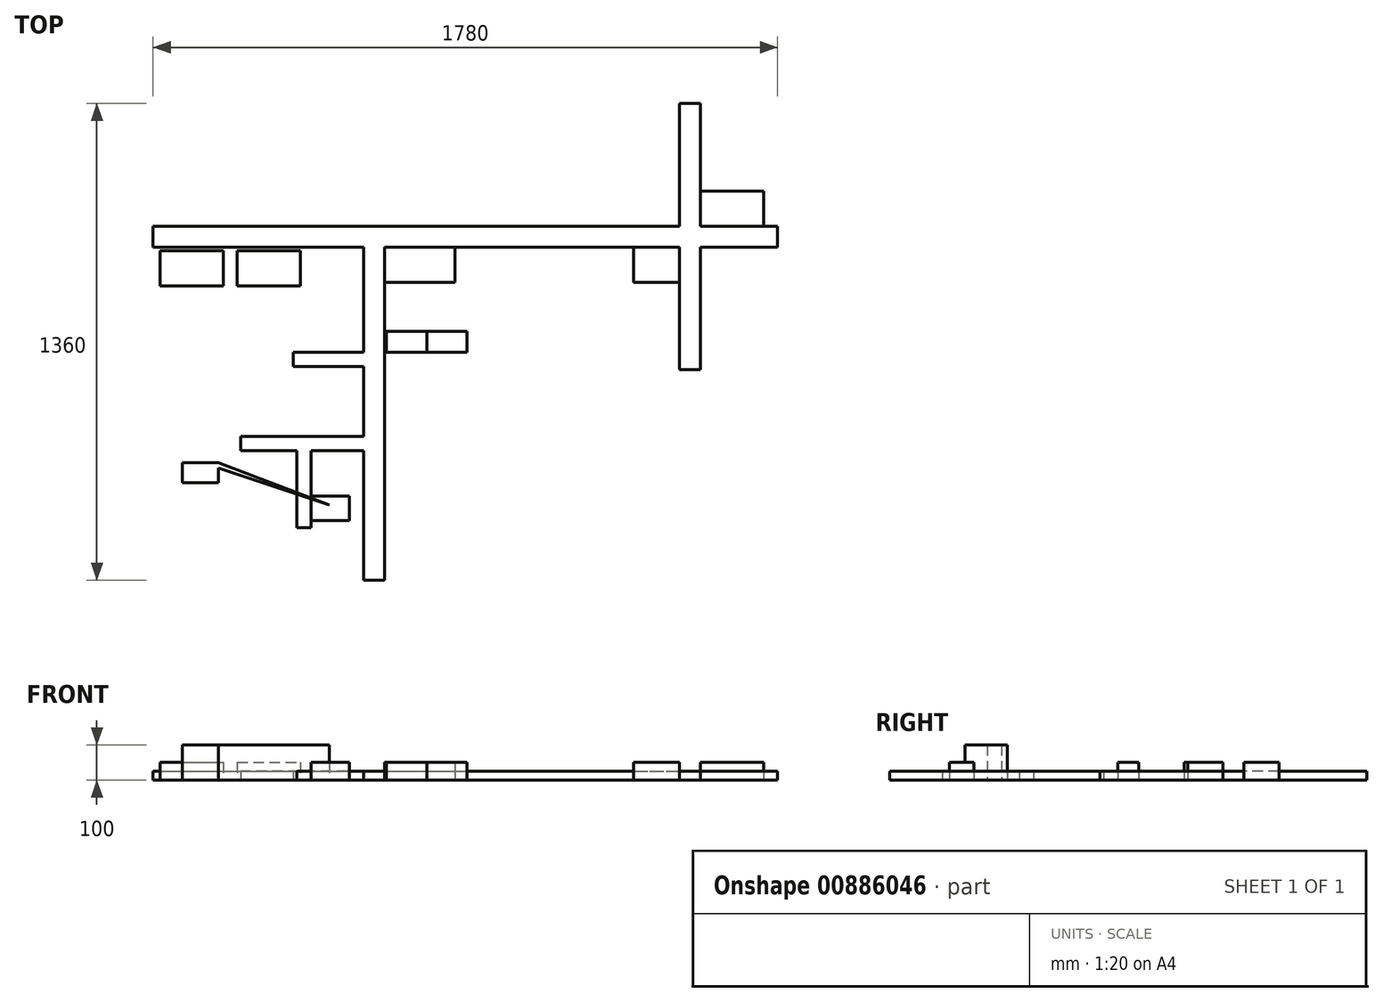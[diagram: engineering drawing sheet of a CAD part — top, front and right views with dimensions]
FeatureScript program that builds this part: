
annotation { "Feature Type Name" : "Feature", "Feature Type Description" : "" }
export const myFeature = defineFeature(function(context is Context, id is Id, definition is map)
    precondition{}
    {
        {
            var Q0;
            Q0=qCreatedBy(makeId("Top.planeOp"),FACE);
            var sketch = newSketch(context, id + "F0", { "sketchPlane" : qUnion([Q0])});
            skLineSegment(sketch, "E0", {"start": v(0, 0) * mm, "end": v(1500, 0) * mm});
            skLineSegment(sketch, "E1", {"start": v(1500, 0) * mm, "end": v(1500, 350) * mm});
            skLineSegment(sketch, "E2", {"start": v(1560, 350) * mm, "end": v(1560, 0) * mm});
            skLineSegment(sketch, "E3", {"start": v(1560, 0) * mm, "end": v(1780, 0) * mm});
            skLineSegment(sketch, "E4", {"start": v(0, -60) * mm, "end": v(600, -60) * mm});
            skLineSegment(sketch, "E5", {"start": v(600, -60) * mm, "end": v(600, -360) * mm});
            skLineSegment(sketch, "E6", {"start": v(600, -360) * mm, "end": v(400, -360) * mm});
            skLineSegment(sketch, "E7", {"start": v(400, -400) * mm, "end": v(600, -400) * mm});
            skLineSegment(sketch, "E8", {"start": v(600, -400) * mm, "end": v(600, -600) * mm});
            skLineSegment(sketch, "E9", {"start": v(600, -600) * mm, "end": v(250, -600) * mm});
            skLineSegment(sketch, "E10", {"start": v(250, -640) * mm, "end": v(410, -640) * mm});
            skLineSegment(sketch, "E11", {"start": v(410, -640) * mm, "end": v(410, -860) * mm});
            skLineSegment(sketch, "E12", {"start": v(450, -860) * mm, "end": v(450, -640) * mm});
            skLineSegment(sketch, "E13", {"start": v(450, -640) * mm, "end": v(600, -640) * mm});
            skLineSegment(sketch, "E14", {"start": v(600, -640) * mm, "end": v(600, -1010) * mm});
            skLineSegment(sketch, "E15", {"start": v(660, -1010) * mm, "end": v(660, -60) * mm});
            skLineSegment(sketch, "E16", {"start": v(660, -60) * mm, "end": v(1500, -60) * mm});
            skLineSegment(sketch, "E17", {"start": v(1500, -60) * mm, "end": v(1500, -410) * mm});
            skLineSegment(sketch, "E18", {"start": v(1560, -410) * mm, "end": v(1560, -60) * mm});
            skLineSegment(sketch, "E19", {"start": v(1560, -60) * mm, "end": v(1780, -60) * mm});
            skLineSegment(sketch, "E20", {"start": v(0, -60) * mm, "end": v(0, 0) * mm});
            skLineSegment(sketch, "E21", {"start": v(1500, -410) * mm, "end": v(1560, -410) * mm});
            skLineSegment(sketch, "E22", {"start": v(1780, 0) * mm, "end": v(1780, -60) * mm});
            skLineSegment(sketch, "E23", {"start": v(1500, 350) * mm, "end": v(1560, 350) * mm});
            skLineSegment(sketch, "E24", {"start": v(600, -1010) * mm, "end": v(660, -1010) * mm});
            skLineSegment(sketch, "E25", {"start": v(410, -860) * mm, "end": v(450, -860) * mm});
            skLineSegment(sketch, "E26", {"start": v(250, -640) * mm, "end": v(250, -600) * mm});
            skLineSegment(sketch, "E27", {"start": v(400, -400) * mm, "end": v(400, -360) * mm});
            skSolve(sketch);
        }
        {
            var Q0;
            Q0 = qSketchRegion(id + "F0", true);
            extrude(context, id + "F1", {"entities" : qUnion([Q0]), "depth" : 25 * mm, "offsetDistance" : 25 * mm});
        }
        {
            var Q0;
            Q0=qCreatedBy(makeId("Top.planeOp"),FACE);
            var sketch = newSketch(context, id + "F2", { "sketchPlane" : qUnion([Q0])});
            skLineSegment(sketch, "E28.0", {"start": v(1560, 0) * mm, "end": v(1740, 0) * mm});
            skLineSegment(sketch, "E28.1", {"start": v(1560, 100) * mm, "end": v(1560, 0) * mm});
            skLineSegment(sketch, "E29", {"start": v(1560, 100) * mm, "end": v(1740, 100) * mm});
            skLineSegment(sketch, "E30", {"start": v(1740, 100) * mm, "end": v(1740, 0) * mm});
            skLineSegment(sketch, "E31.0", {"start": v(1370, -60) * mm, "end": v(1500, -60) * mm});
            skLineSegment(sketch, "E32", {"start": v(1500, -60) * mm, "end": v(1500, -160) * mm});
            skLineSegment(sketch, "E33", {"start": v(1500, -160) * mm, "end": v(1370, -160) * mm});
            skLineSegment(sketch, "E34", {"start": v(1370, -160) * mm, "end": v(1370, -60) * mm});
            skLineSegment(sketch, "E35.0", {"start": v(660, -160) * mm, "end": v(660, -60) * mm});
            skLineSegment(sketch, "E36", {"start": v(660, -60) * mm, "end": v(860, -60) * mm});
            skLineSegment(sketch, "E37", {"start": v(860, -60) * mm, "end": v(860, -160) * mm});
            skLineSegment(sketch, "E38", {"start": v(860, -160) * mm, "end": v(660, -160) * mm});
            skLineSegment(sketch, "E39.bottom", {"start": v(665, -360) * mm, "end": v(895, -360) * mm});
            skLineSegment(sketch, "E39.top", {"start": v(665, -300) * mm, "end": v(895, -300) * mm});
            skLineSegment(sketch, "E39.left", {"start": v(665, -360) * mm, "end": v(665, -300) * mm});
            skLineSegment(sketch, "E39.right", {"start": v(895, -360) * mm, "end": v(895, -300) * mm});
            skLineSegment(sketch, "E40", {"start": v(780, -300) * mm, "end": v(780, -360) * mm});
            skLineSegment(sketch, "E41.0", {"start": v(450, -840) * mm, "end": v(450, -770) * mm});
            skLineSegment(sketch, "E42", {"start": v(450, -770) * mm, "end": v(560, -770) * mm});
            skLineSegment(sketch, "E43", {"start": v(560, -770) * mm, "end": v(560, -840) * mm});
            skLineSegment(sketch, "E44", {"start": v(560, -840) * mm, "end": v(450, -840) * mm});
            skLineSegment(sketch, "E45.bottom", {"start": v(20, -70) * mm, "end": v(200, -70) * mm});
            skLineSegment(sketch, "E45.top", {"start": v(20, -170) * mm, "end": v(200, -170) * mm});
            skLineSegment(sketch, "E45.left", {"start": v(20, -70) * mm, "end": v(20, -170) * mm});
            skLineSegment(sketch, "E45.right", {"start": v(200, -70) * mm, "end": v(200, -170) * mm});
            skLineSegment(sketch, "E46.bottom", {"start": v(240, -70) * mm, "end": v(420, -70) * mm});
            skLineSegment(sketch, "E46.top", {"start": v(240, -170) * mm, "end": v(420, -170) * mm});
            skLineSegment(sketch, "E46.left", {"start": v(240, -70) * mm, "end": v(240, -170) * mm});
            skLineSegment(sketch, "E46.right", {"start": v(420, -70) * mm, "end": v(420, -170) * mm});
            skSolve(sketch);
        }
        {
            var Q0;
            Q0=makeQuery(id+"F2.imprint","IMPRINT",FACE,{"disambiguationData":[TD([[makeQuery(id+"F2.imprint","IMPRINT",EDGE,{"derivedFrom":sQuery(id+"F2.wireOp",EDGE,"E45.bottom")}),-1.0]])]});
            var Q1;
            Q1=makeQuery(id+"F2.imprint","IMPRINT",FACE,{"disambiguationData":[TD([[makeQuery(id+"F2.imprint","IMPRINT",EDGE,{"derivedFrom":sQuery(id+"F2.wireOp",EDGE,"E46.bottom")}),-1.0]])]});
            var Q2;
            Q2=makeQuery(id+"F2.imprint","IMPRINT",FACE,{"disambiguationData":[TD([[makeQuery(id+"F2.imprint","IMPRINT",EDGE,{"derivedFrom":sQuery(id+"F2.wireOp",EDGE,"E35.0")}),-1.0]])]});
            var Q3;
            {var subQ0=sQuery(id+"F2.wireOp",EDGE,"E39.left");Q3=makeQuery(id+"F2.imprint","IMPRINT",FACE,{"disambiguationData":[TD([[makeQuery(id+"F2.imprint","IMPRINT",EDGE,{"derivedFrom":subQ0}),-1.0]])]});}
            var Q4;
            Q4=makeQuery(id+"F2.imprint","IMPRINT",FACE,{"disambiguationData":[TD([[makeQuery(id+"F2.imprint","IMPRINT",EDGE,{"derivedFrom":sQuery(id+"F2.wireOp",EDGE,"E31.0")}),-1.0]])]});
            var Q5;
            Q5=makeQuery(id+"F2.imprint","IMPRINT",FACE,{"disambiguationData":[TD([[makeQuery(id+"F2.imprint","IMPRINT",EDGE,{"derivedFrom":sQuery(id+"F2.wireOp",EDGE,"E28.0")}),1.0]])]});
            var Q6;
            Q6=makeQuery(id+"F2.imprint","IMPRINT",FACE,{"disambiguationData":[TD([[makeQuery(id+"F2.imprint","IMPRINT",EDGE,{"derivedFrom":sQuery(id+"F2.wireOp",EDGE,"E41.0")}),-1.0]])]});
            extrude(context, id + "F3", {"entities" : qUnion([Q0, Q1, Q2, Q3, Q4, Q5, Q6]), "operationType" : NewBodyOperationType.ADD, "depth" : 50 * mm, "offsetDistance" : 25 * mm});
        }
        {
            var Q0;
            {var subQ0=sQuery(id+"F2.wireOp",EDGE,"E39.right");Q0=makeQuery(id+"F2.imprint","IMPRINT",FACE,{"disambiguationData":[TD([[makeQuery(id+"F2.imprint","IMPRINT",EDGE,{"derivedFrom":subQ0}),1.0]])]});}
            extrude(context, id + "F4", {"entities" : qUnion([Q0]), "depth" : 50 * mm, "offsetDistance" : 25 * mm});
        }
        {
            var Q0;
            Q0=qCreatedBy(makeId("Top.planeOp"),FACE);
            var sketch = newSketch(context, id + "F5", { "sketchPlane" : qUnion([Q0])});
            skLineSegment(sketch, "E47.bottom", {"start": v(83.83, -674.5) * mm, "end": v(186.66, -674.5) * mm});
            skLineSegment(sketch, "E47.top", {"start": v(83.83, -731.75) * mm, "end": v(186.66, -731.75) * mm});
            skLineSegment(sketch, "E47.left", {"start": v(83.83, -674.5) * mm, "end": v(83.83, -731.75) * mm});
            skLineSegment(sketch, "E48", {"start": v(186.66, -674.5) * mm, "end": v(501.86, -795.42) * mm});
            skLineSegment(sketch, "E49", {"start": v(501.86, -795.42) * mm, "end": v(186.66, -690.63) * mm});
            skLineSegment(sketch, "E50", {"start": v(186.66, -690.63) * mm, "end": v(186.66, -731.75) * mm});
            skSolve(sketch);
        }
        {
            var Q0;
            Q0 = qSketchRegion(id + "F5", true);
            extrude(context, id + "F6", {"entities" : qUnion([Q0]), "depth" : 100 * mm, "offsetDistance" : 25 * mm});
        }
    });
